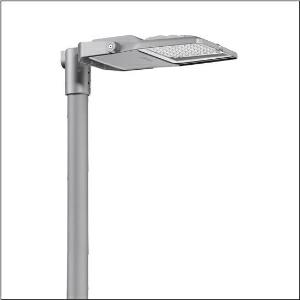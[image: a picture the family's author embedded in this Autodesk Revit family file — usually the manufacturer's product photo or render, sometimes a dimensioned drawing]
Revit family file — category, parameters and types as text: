
# Revit family: floodlight_fl_21_mini___pl33t_5xa7775d2f3a_2fb5
name_source: partatom
category: Lighting Fixtures
units: mm (PartAtom-declared; Revit-internal decimal feet)

## family parameters
Cut with Voids When Loaded = No
Host = Face
Light Source = No
Part Type = Normal
Room Calculation Point = No
Round Connector Dimension = Use Diameter
Shared = No

## types (1)
- --- (1 x LED, 17630 lm, 142.9 W, 3000K)
    Apparent Load = 143 VA
    CIE Flux Codes = 26 75 99 100 100
    Color Rendering = 70
    Color Temperature = 3000K
    Default Elevation = 1800 mm
    Description = Floodlight FL 21 mini, floodlight, primary light control with lens, of PMMA, primary optical cover: protective disc, of toughened safety glass, transparent, light distribution: PL33T, light emission: direct distribution, installation type: surface-mounted, LED, High Power LED, rated luminous flux: 17.630lm, luminous efficacy: 123lm/W, light colour: 730, colour temperature: 3000K, control: flexible luminous flux parameterisation, time-dependent luminous flux control, constant luminous flux control, overheat protection, presetting dimming logarithmic, with terminal, 6-pole, mains connection: 220..240V, AC, 50/60Hz, start of lifetime: 143W, end of service life: 151W, reduction: 63W, luminaire housing, of diecast aluminium, powder-coated, Siteco® metallic grey (DB 702S), corrosivity category C5 mid according to DIN EN ISO 12944, sealing non-destructively replaceable, please order mast flange separately, mast bracket, of steel, galvanised, powder-coated, Siteco® metallic grey (DB 702S), Smart Interface above, protection rating (complete): IP66, insulation class (complete): insulation class II (safety insulation), certification: CE, ENEC, VDE, protection symbol: D, impact resistance: IK08, permissible operating ambient temperature: -40..+40°C, permissible operating ambient temperature for outdoor applications: -40..+50°C, standard: DIN EN 12944, LABS conformity tested according to VDMA 24364:2018-05, packaging unit: 1 piece

Light Distribution: PL33T
    Height = 70 mm
    Lamp = 1 x LED
    Lamp Light Flux = 17630 lm
    Lamp Power = 142.9 W
    Lamp count = 1
    Length = 485 mm
    Luminous efficacy = 123 lm/W
    Manufacturer = Siteco
    ModVariant = No
    Model = 5XA7775D2F3A
    Number of Poles = 1
    OnlyDefault = Yes
    Power Factor = 1
    Product Name = Floodlight FL 21 mini | PL33T
    Product group = floodlight | pylon annexe
    ProductGroupID = 6200
    Protection Class = Protection class II
    Protection Degree = IP 66
    RLX_Detail_Level = 1
    RLX_Emergency_Light_Flux = 0 lm
    RLX_Emergency_Type = 0
    RLX_Emergency_Type_DB = No
    RlxData = <blob elided: 101069 chars, md5=de0dcb58>
    Socket = socket
    Standby Power = 0 W
    System Light Flux = 17630 lm
    System Power = 143 W
    Type Comments = factory setting: luminous flux: 100 % | dim-lin: 254 | 730 mA
    Type Image = l_1007125.jpg
    URL = http://relux.com
    VarID = @adj_098563
    Voltage = 0 V
    Weight = 0.00 kg
    Width = 337 mm

## geometry (parser evidence)
native form markers: Blend x4, Sweep x12
no freeform markers — native parametric forms only
